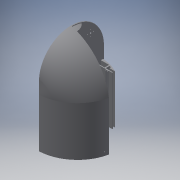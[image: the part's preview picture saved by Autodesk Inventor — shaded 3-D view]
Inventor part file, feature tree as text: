
AUTODESK INVENTOR PART (.ipt)
format: ipt  version: 2019 (Build 230136000, 136)  size: 806,400 bytes
history: native  units: mm
features: extrude x18, sketch x17, other x7, projected_geometry x3, reference x2, loft x1, shell x1, mirror x1, fillet x1
ambient origin geometry x8: Origin, YZ Plane, XZ Plane, XY Plane, X Axis, Y Axis, Z Axis, Center Point
bodies: Body1 (feature_tree)
feature tree (51):
  sketch  "Эскиз4"
  other  "РабПлоскость1"
  sketch  "Эскиз5"
  loft  "Лофт1"
  extrude  "Выдавливание2"  Depth=100.0mm
  shell  "Оболочка1"  Thickness=17.0mm
  sketch  "Эскиз21"
  extrude  "Выдавливание15"  Depth=4.0mm
  extrude  "Выдавливание16"  Depth=35.0mm
  other  "РабПлоскость7"
  sketch  "Эскиз23"
  extrude  "Выдавливание17"  TaperAngle=0.0deg  [1 undecoded]
  extrude  "Выдавливание18"  TaperAngle=0.0deg  [1 undecoded]
  sketch  "Эскиз24"
  extrude  "Выдавливание19"  TaperAngle=0.0deg  [1 undecoded]
  extrude  "Выдавливание20"  Depth=130.0mm TaperAngle=0.0deg
  extrude  "Выдавливание21"  Depth=5.0mm
  mirror  "Зеркальное отражение2"
  other  "РабПлоскость12"
  extrude  "Выдавливание57"  Depth=2.0mm
  sketch  "Эскиз84"
  extrude  "Выдавливание75"  Depth=2.0mm
  extrude  "Выдавливание76"  Depth=2.0mm
  extrude  "Выдавливание77"  Depth=20.0mm
  extrude  "Выдавливание95"  Depth=10.0mm TaperAngle=0.0deg
  extrude  "Выдавливание96"  Depth=10.0mm TaperAngle=0.0deg
  extrude  "Выдавливание97"  Depth=143.802871mm
  fillet  "Сопряжение3"  [1 undecoded]
  extrude  "Выдавливание98"  Depth=1.0mm TaperAngle=0.0deg
  extrude  "Выдавливание101"  Depth=5.0mm
  other  "РабПлоскость25"
  extrude  "Выдавливание102"  Depth=5.0mm
  sketch  "Эскиз6"
  projected_geometry  "Спроецированная петля1"
  sketch  "Эскиз22"
  sketch  "Эскиз25"
  sketch  "Эскиз61"
  sketch  "Эскиз87"
  sketch  "Эскиз109"
  sketch  "Эскиз110"
  projected_geometry  "Спроецированная петля42"
  sketch  "Эскиз111"
  projected_geometry  "Спроецированная петля43"
  sketch  "Эскиз114"
  sketch  "Эскиз117"
  sketch  "Эскиз118"
  reference  "Ссылка1"
  reference  "Ссылка2"
  other  "<userpath>\Desktop\RobotFix1\робот\робот - сборка фулл.iam"
  other  "робот - сборка фулл.iam"
  other  "крепление-стенки:1"
note: 4 required parameter values undecoded (feature->parameter linkage not recoverable at this tier; creation-order binding heuristic only, values carry confidence <= 0.55)
